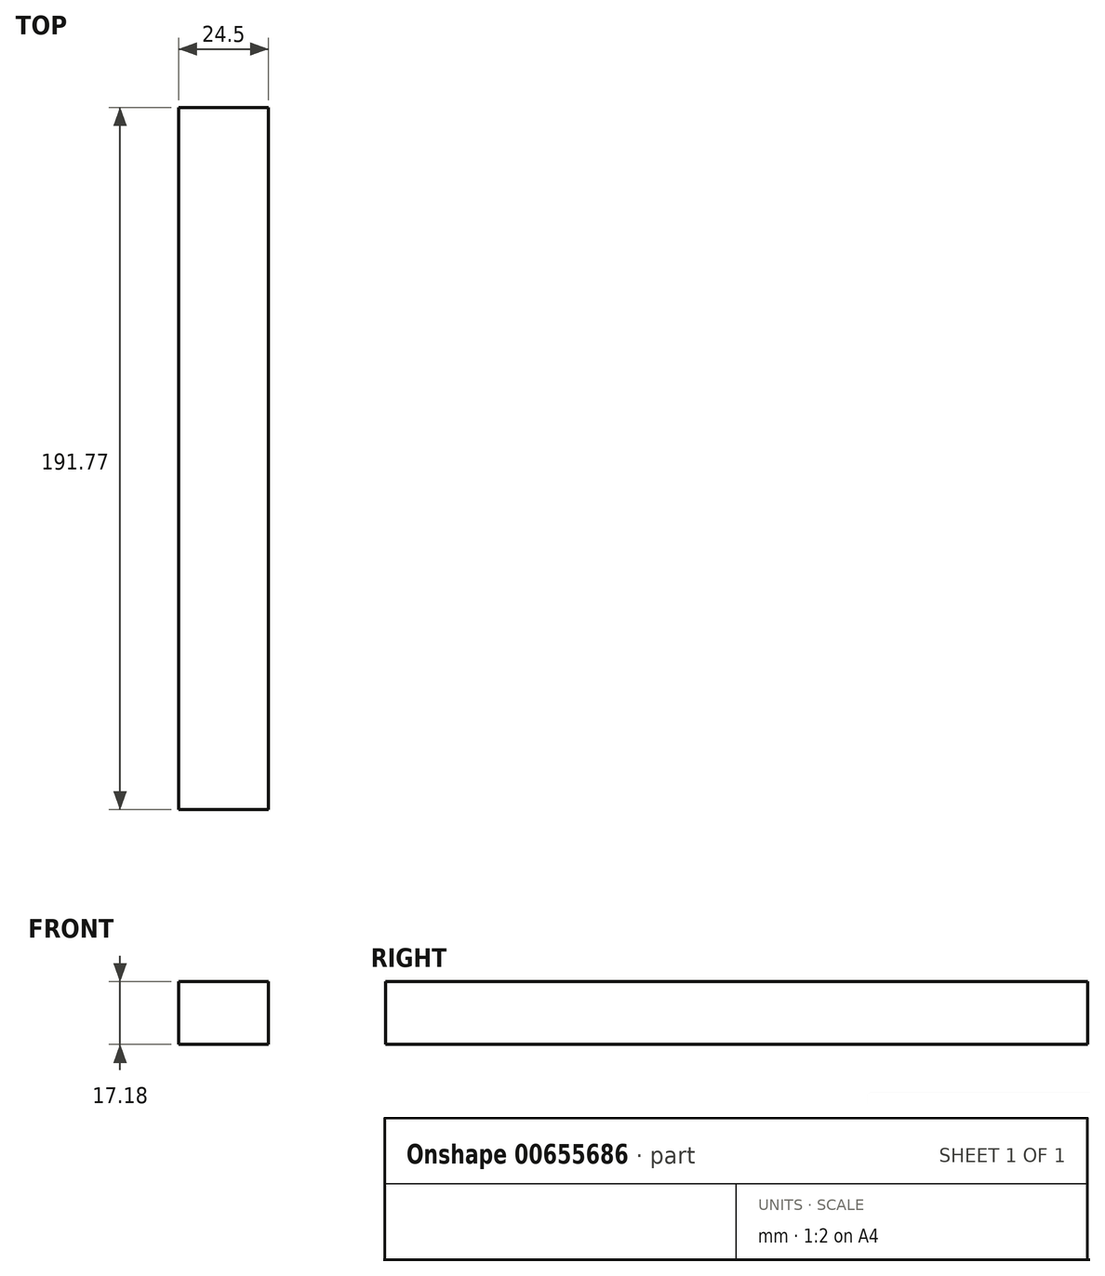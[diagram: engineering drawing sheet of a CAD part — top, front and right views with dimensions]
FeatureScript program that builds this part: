
annotation { "Feature Type Name" : "Feature", "Feature Type Description" : "" }
export const myFeature = defineFeature(function(context is Context, id is Id, definition is map)
    precondition{}
    {
        {
            var Q0;
            Q0=qCreatedBy(makeId("Front.planeOp"),FACE);
            var sketch = newSketch(context, id + "F0", { "sketchPlane" : qUnion([Q0])});
            skLineSegment(sketch, "E0.bottom", {"start": v(-9.58, 4.77) * mm, "end": v(9.84, 4.77) * mm});
            skLineSegment(sketch, "E0.top", {"start": v(-9.58, -7.33) * mm, "end": v(9.84, -7.33) * mm});
            skLineSegment(sketch, "E0.left", {"start": v(-9.58, 4.77) * mm, "end": v(-9.58, -7.33) * mm});
            skLineSegment(sketch, "E0.right", {"start": v(9.84, 4.77) * mm, "end": v(9.84, -7.33) * mm});
            skLineSegment(sketch, "E1.bottom", {"start": v(-12.12, 7.31) * mm, "end": v(12.38, 7.31) * mm});
            skLineSegment(sketch, "E1.top", {"start": v(-12.12, -9.87) * mm, "end": v(12.38, -9.87) * mm});
            skLineSegment(sketch, "E1.left", {"start": v(-12.12, 7.31) * mm, "end": v(-12.12, -9.87) * mm});
            skLineSegment(sketch, "E1.right", {"start": v(12.38, 7.31) * mm, "end": v(12.38, -9.87) * mm});
            skSolve(sketch);
        }
        {
            var Q0;
            Q0=makeQuery(id+"F0.imprint","IMPRINT",FACE,{"disambiguationData":[TD([[makeQuery(id+"F0.imprint","IMPRINT",EDGE,{"derivedFrom":sQuery(id+"F0.wireOp",EDGE,"E0.bottom")}),1.0]])]});
            var Q1;
            Q1=makeQuery(id+"F0.imprint","IMPRINT",FACE,{"disambiguationData":[TD([[makeQuery(id+"F0.imprint","IMPRINT",EDGE,{"derivedFrom":sQuery(id+"F0.wireOp",EDGE,"E0.bottom")}),-1.0]])]});
            extrude(context, id + "F1", {"entities" : qUnion([Q0, Q1]), "depth" : 182.88 * mm, "offsetDistance" : 25.4 * mm});
        }
        {
            var Q0;
            Q0=makeQuery(id+"F1.opExtrude","CAP_FACE",FACE,{"disambiguationData":[OSD([sQuery(id+"F0.wireOp",EDGE,"E1.bottom"),sQuery(id+"F0.wireOp",EDGE,"E1.top"),sQuery(id+"F0.wireOp",EDGE,"E1.left"),sQuery(id+"F0.wireOp",EDGE,"E1.right")])],"isStart":false});
            extrude(context, id + "F2", {"entities" : qUnion([Q0]), "operationType" : NewBodyOperationType.ADD, "depth" : 8.9 * mm, "offsetDistance" : 25.4 * mm});
        }
    });
